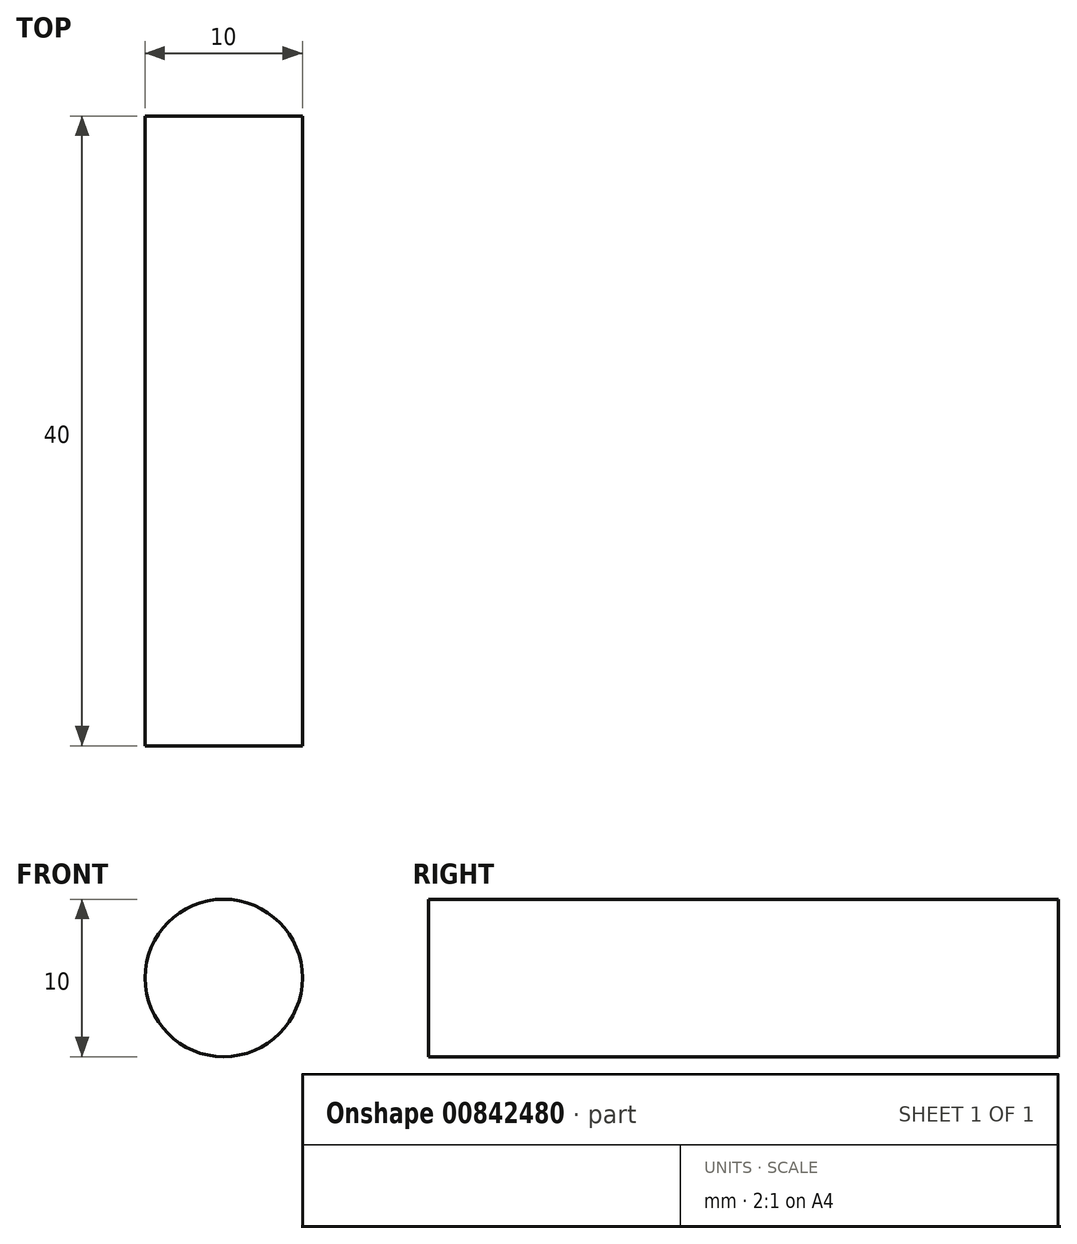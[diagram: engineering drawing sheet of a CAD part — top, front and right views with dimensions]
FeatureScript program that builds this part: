
annotation { "Feature Type Name" : "Feature", "Feature Type Description" : "" }
export const myFeature = defineFeature(function(context is Context, id is Id, definition is map)
    precondition{}
    {
        {
            var Q0;
            Q0=qCreatedBy(makeId("Front.planeOp"),FACE);
            var sketch = newSketch(context, id + "F0", { "sketchPlane" : qUnion([Q0])});
            skCircle(sketch, "E0", {"center": v(0, 0) * mm, "radius": 5 * mm});
            skSolve(sketch);
        }
        {
            var Q0;
            Q0 = qSketchRegion(id + "F0", true);
            extrude(context, id + "F1", {"entities" : qUnion([Q0]), "depth" : 40 * mm, "offsetDistance" : 25 * mm});
        }
    });
